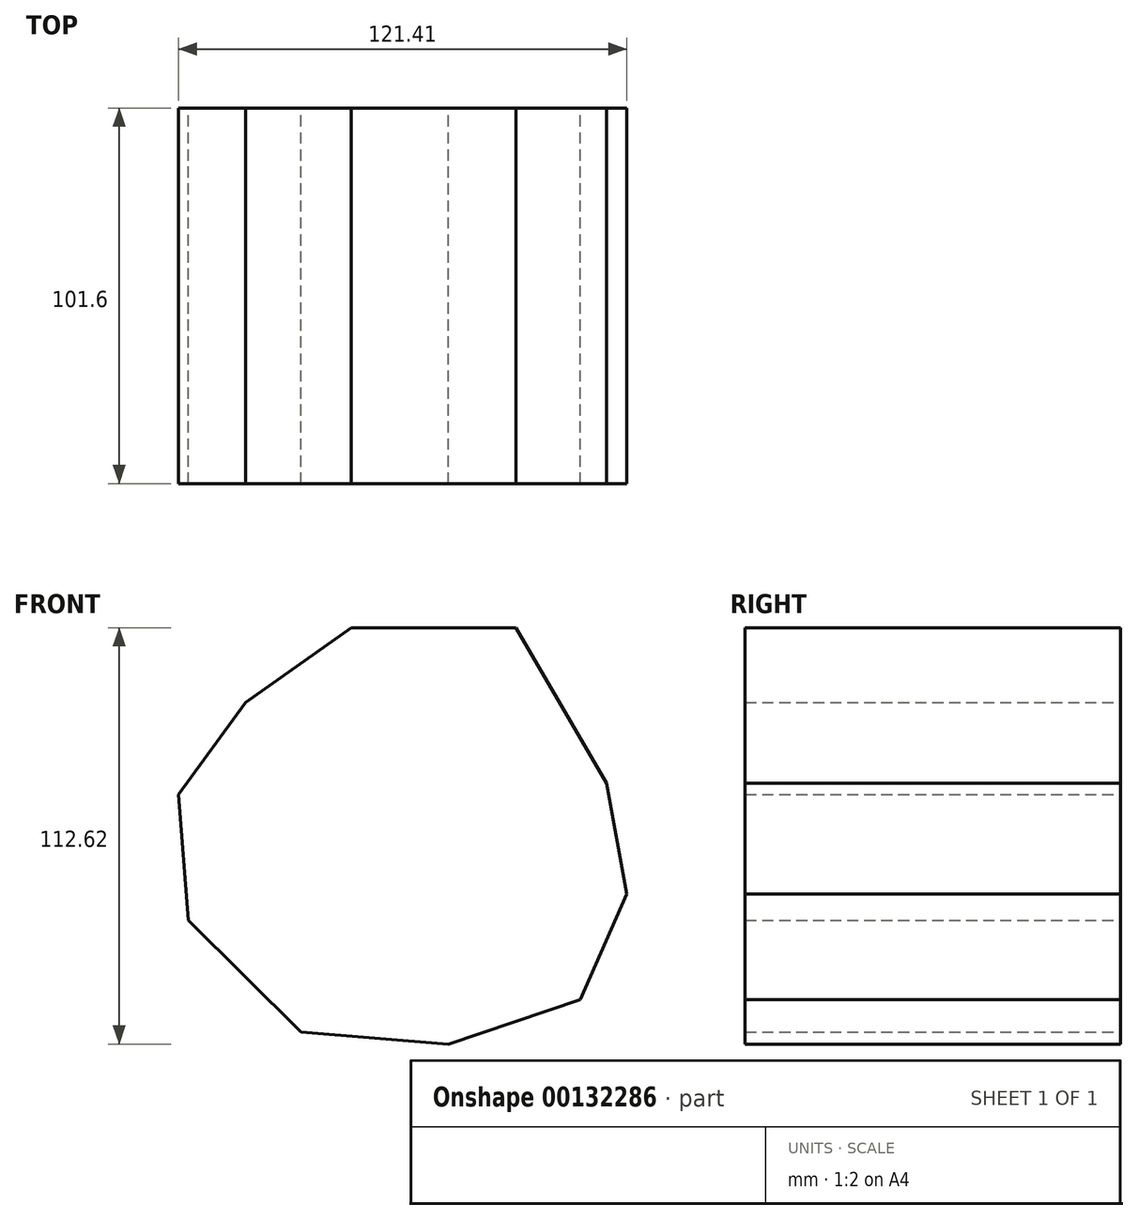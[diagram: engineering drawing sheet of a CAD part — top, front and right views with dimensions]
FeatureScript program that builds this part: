
annotation { "Feature Type Name" : "Feature", "Feature Type Description" : "" }
export const myFeature = defineFeature(function(context is Context, id is Id, definition is map)
    precondition{}
    {
        {
            var Q0;
            Q0=qCreatedBy(makeId("Front.planeOp"),FACE);
            var sketch = newSketch(context, id + "F0", { "sketchPlane" : qUnion([Q0])});
            skLineSegment(sketch, "E0", {"start": v(-16.09, 45.05) * mm, "end": v(28.53, 45.05) * mm});
            skLineSegment(sketch, "E1", {"start": v(-16.09, 45.05) * mm, "end": v(-44.62, 24.88) * mm});
            skLineSegment(sketch, "E2", {"start": v(-44.62, 24.88) * mm, "end": v(-62.85, 0) * mm});
            skLineSegment(sketch, "E3", {"start": v(-62.85, 0) * mm, "end": v(-60.06, -34.1) * mm});
            skLineSegment(sketch, "E4", {"start": v(-60.06, -34.1) * mm, "end": v(-29.6, -64.35) * mm});
            skLineSegment(sketch, "E5", {"start": v(-29.6, -64.35) * mm, "end": v(10.3, -67.57) * mm});
            skLineSegment(sketch, "E6", {"start": v(10.3, -67.57) * mm, "end": v(45.9, -55.56) * mm});
            skLineSegment(sketch, "E7", {"start": v(45.9, -55.56) * mm, "end": v(58.56, -27.03) * mm});
            skLineSegment(sketch, "E8", {"start": v(58.56, -27.03) * mm, "end": v(52.98, 3) * mm});
            skLineSegment(sketch, "E9", {"start": v(52.98, 3) * mm, "end": v(28.53, 45.05) * mm});
            skSolve(sketch);
        }
        {
            var Q0;
            Q0 = qSketchRegion(id + "F0", true);
            extrude(context, id + "F1", {"entities" : qUnion([Q0]), "depth" : 101.6 * mm});
        }
    });
